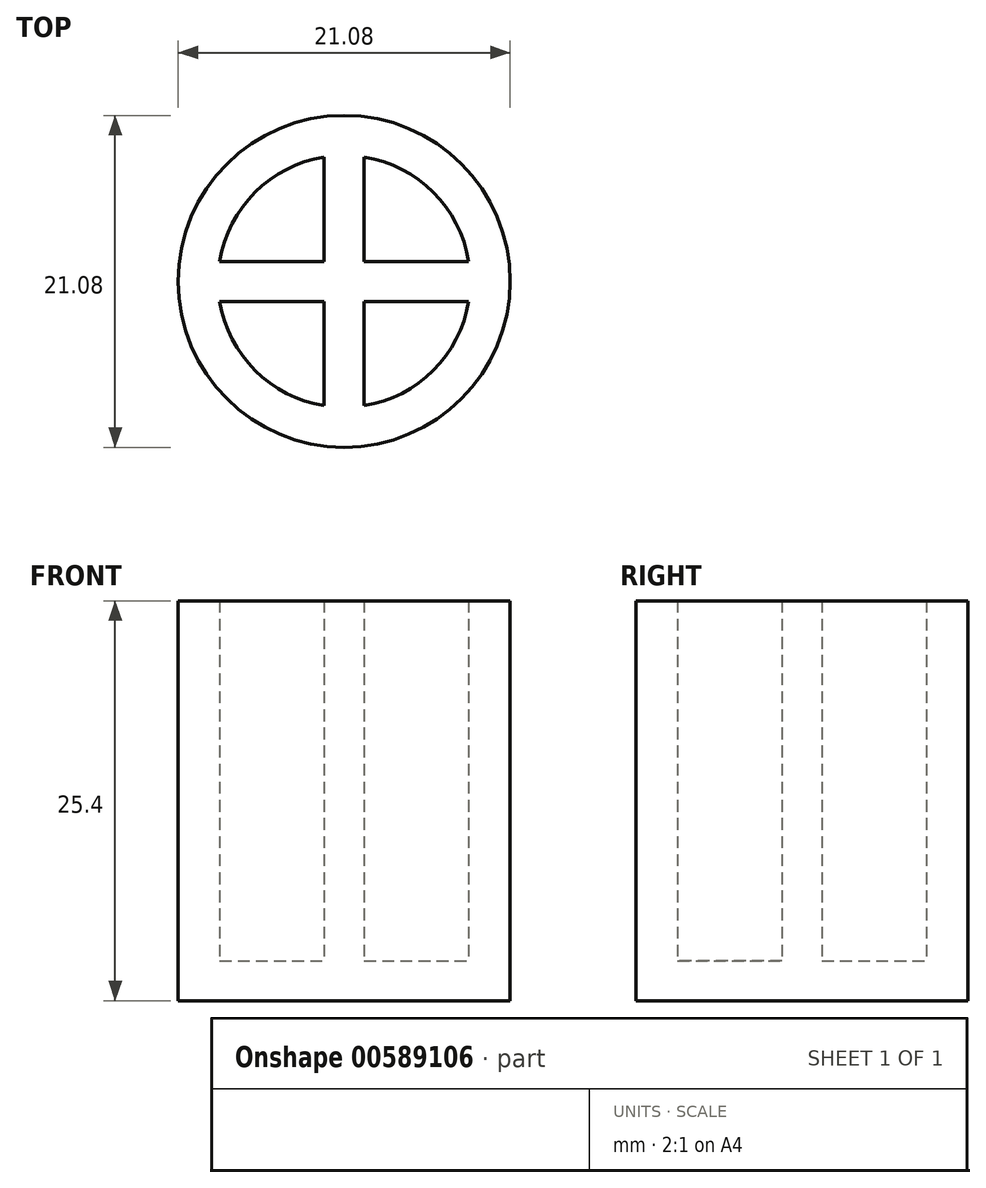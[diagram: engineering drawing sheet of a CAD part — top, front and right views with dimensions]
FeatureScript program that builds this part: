
annotation { "Feature Type Name" : "Feature", "Feature Type Description" : "" }
export const myFeature = defineFeature(function(context is Context, id is Id, definition is map)
    precondition{}
    {
        {
            var Q0;
            Q0=qCreatedBy(makeId("Top.planeOp"),FACE);
            var sketch = newSketch(context, id + "F0", { "sketchPlane" : qUnion([Q0])});
            skCircle(sketch, "E0", {"center": v(0, 0) * mm, "radius": 10.54 * mm});
            skSolve(sketch);
        }
        {
            var Q0;
            Q0=qSketchRegion(id+"F0",true);
            extrude(context, id + "F1", {"entities" : qUnion([Q0]), "depth" : 25.4 * mm, "offsetDistance" : 25.4 * mm});
        }
        {
            var Q0;
            Q0=makeQuery(id+"F1.opExtrude","CAP_FACE",FACE,{"disambiguationData":[OSD([sQuery(id+"F0.wireOp",EDGE,"E0")])],"isStart":false});
            var sketch = newSketch(context, id + "F2", { "sketchPlane" : qUnion([Q0])});
            skCircle(sketch, "E1", {"center": v(0, 0) * mm, "radius": 8 * mm});
            skSolve(sketch);
        }
        {
            var Q0;
            Q0=qSketchRegion(id+"F2",true);
            extrude(context, id + "F3", {"entities" : qUnion([Q0]), "operationType" : NewBodyOperationType.REMOVE, "oppositeDirection" : true, "depth" : 22.86 * mm, "offsetDistance" : 25.4 * mm});
        }
        {
            var Q0;
            Q0=makeQuery(id+"F3.boolean.opBoolean","COPY",FACE,{"derivedFrom":makeQuery(id+"F3.opExtrude","CAP_FACE",FACE,{"disambiguationData":[OSD([sQuery(id+"F2.wireOp",EDGE,"E1")])],"isStart":false})});
            var sketch = newSketch(context, id + "F4", { "sketchPlane" : qUnion([Q0])});
            skLineSegment(sketch, "E2", {"start": v(-1.27, -7.9) * mm, "end": v(-1.27, 7.9) * mm});
            skLineSegment(sketch, "E3", {"start": v(1.27, -7.9) * mm, "end": v(1.27, 7.9) * mm});
            skLineSegment(sketch, "E4", {"start": v(-7.9, 1.27) * mm, "end": v(7.9, 1.27) * mm});
            skLineSegment(sketch, "E5", {"start": v(-7.9, -1.27) * mm, "end": v(7.9, -1.27) * mm});
            skSolve(sketch);
        }
        {
            var Q0;
            Q0 = qSketchRegion(id + "F4", true);
            var Q1;
            {var subQ0=sQuery(id+"F4.wireOp",EDGE,"E5");var subQ1=sQuery(id+"F4.wireOp",EDGE,"E3");var subQ2=makeQuery(id+"F4.imprint","INTERSECT",VERTEX,{"derivedFrom":[subQ1,subQ0]});Q1=makeQuery(id+"F4.imprint","IMPRINT",FACE,{"disambiguationData":[TD([[makeQuery(id+"F4.imprint","IMPRINT",EDGE,{"disambiguationData":[TD([[subQ2,-1.0]])],"derivedFrom":subQ1}),-1.0]])]});}
            var Q2;
            {var subQ0=sQuery(id+"F4.wireOp",EDGE,"E2");var subQ1=makeQuery(id+"F3.boolean.opBoolean","COPY",EDGE,{"derivedFrom":makeQuery(id+"F3.opExtrude","CAP_EDGE",EDGE,{"disambiguationData":[OSD([sQuery(id+"F2.wireOp",EDGE,"E1")])],"isStart":false})});var subQ2=makeQuery(id+"F4.imprint","INTERSECT",VERTEX,{"disambiguationData":[OD(1.0)],"derivedFrom":[subQ1,subQ0]});Q2=makeQuery(id+"F4.imprint","IMPRINT",FACE,{"disambiguationData":[TD([[makeQuery(id+"F4.imprint","IMPRINT",EDGE,{"disambiguationData":[TD([[subQ2,1.0]])],"derivedFrom":subQ0}),-1.0]])]});}
            var Q3;
            {var subQ0=sQuery(id+"F4.wireOp",EDGE,"E5");var subQ1=sQuery(id+"F4.wireOp",EDGE,"E2");var subQ2=makeQuery(id+"F4.imprint","INTERSECT",VERTEX,{"derivedFrom":[subQ1,subQ0]});Q3=makeQuery(id+"F4.imprint","IMPRINT",FACE,{"disambiguationData":[TD([[makeQuery(id+"F4.imprint","IMPRINT",EDGE,{"disambiguationData":[TD([[subQ2,-1.0]])],"derivedFrom":subQ1}),1.0]])]});}
            var Q4;
            {var subQ0=sQuery(id+"F4.wireOp",EDGE,"E2");var subQ1=makeQuery(id+"F3.boolean.opBoolean","COPY",EDGE,{"derivedFrom":makeQuery(id+"F3.opExtrude","CAP_EDGE",EDGE,{"disambiguationData":[OSD([sQuery(id+"F2.wireOp",EDGE,"E1")])],"isStart":false})});var subQ2=makeQuery(id+"F4.imprint","INTERSECT",VERTEX,{"disambiguationData":[OD(0.0)],"derivedFrom":[subQ1,subQ0]});Q4=makeQuery(id+"F4.imprint","IMPRINT",FACE,{"disambiguationData":[TD([[makeQuery(id+"F4.imprint","IMPRINT",EDGE,{"disambiguationData":[TD([[subQ2,-1.0]])],"derivedFrom":subQ0}),-1.0]])]});}
            extrude(context, id + "F5", {"entities" : qUnion([Q0, Q1, Q2, Q3, Q4]), "operationType" : NewBodyOperationType.ADD, "depth" : 22.86 * mm, "offsetDistance" : 25.4 * mm});
        }
    });
